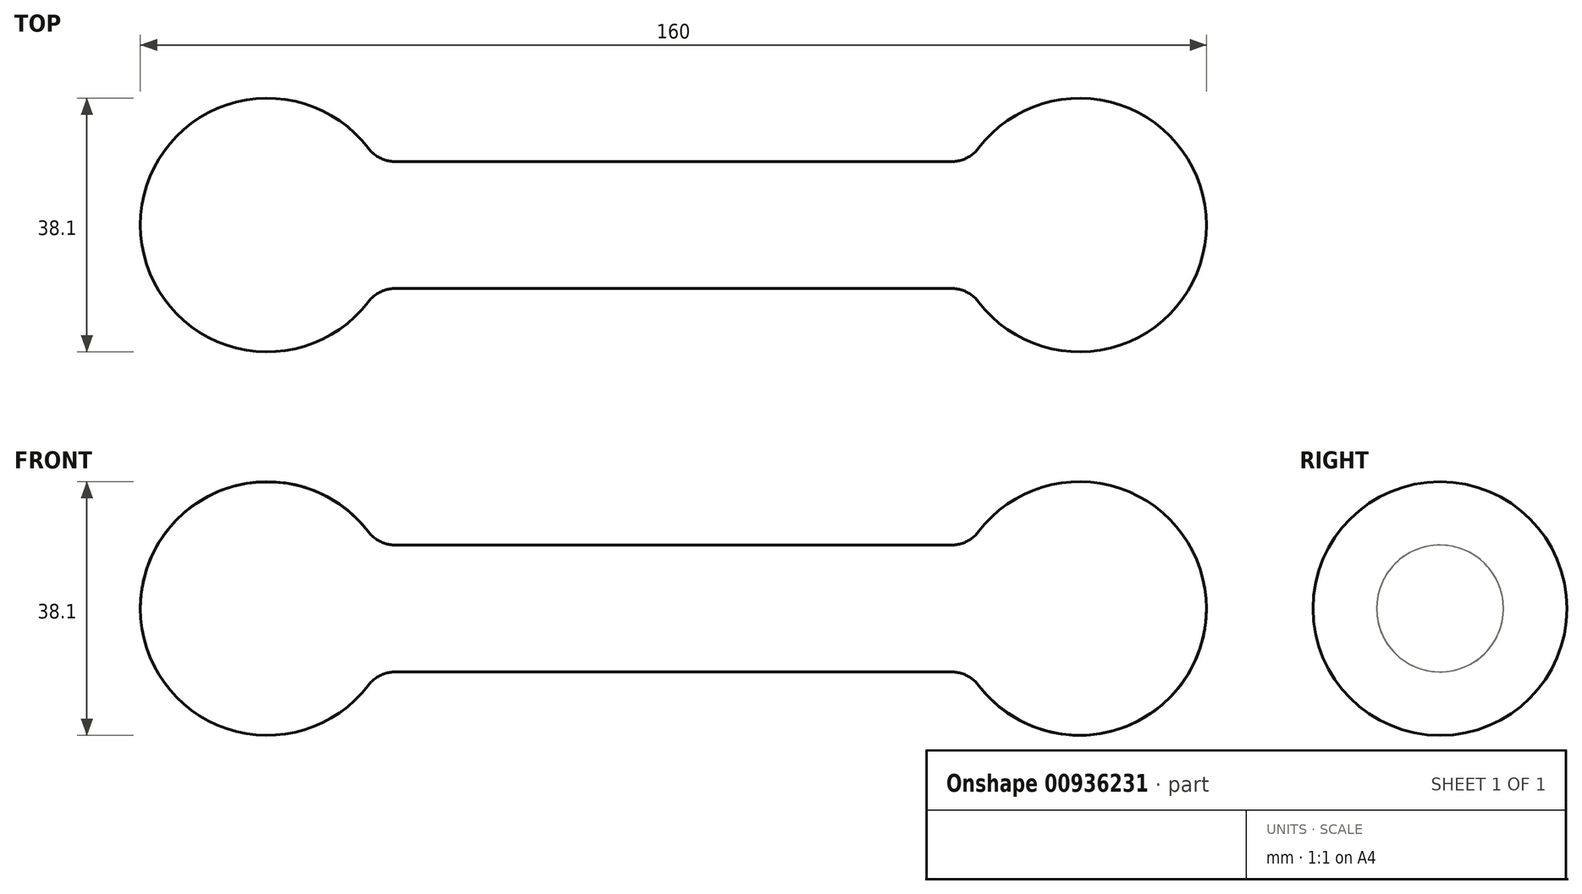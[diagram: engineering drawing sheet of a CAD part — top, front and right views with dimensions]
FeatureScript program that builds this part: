
annotation { "Feature Type Name" : "Feature", "Feature Type Description" : "" }
export const myFeature = defineFeature(function(context is Context, id is Id, definition is map)
    precondition{}
    {
        {
            var Q0;
            Q0=qCreatedBy(makeId("Front.planeOp"),FACE);
            var sketch = newSketch(context, id + "F0", { "sketchPlane" : qUnion([Q0])});
            skArc(sketch, "E0", {"start": v(-44.45, 9.53) * mm, "mid": v(-65.88, 18.4) * mm, "end": v(-80, 0) * mm});
            skLineSegment(sketch, "E1", {"start": v(-91.96, 0) * mm, "end": v(97.12, 0) * mm, "construction": true});
            skLineSegment(sketch, "E2", {"start": v(-44.45, 9.53) * mm, "end": v(0, 9.53) * mm});
            skPoint(sketch, "E3.orphan", {"position": v(-41.9, 0) * mm});
            skArc(sketch, "E4.MirrorCS", {"start": v(44.45, 9.53) * mm, "mid": v(65.88, 18.4) * mm, "end": v(80, 0) * mm});
            skLineSegment(sketch, "E5.MirrorCS", {"start": v(44.45, 9.53) * mm, "end": v(0, 9.53) * mm});
            skLineSegment(sketch, "E6", {"start": v(-80, 0) * mm, "end": v(80, 0) * mm});
            skSolve(sketch);
        }
        {
            var Q0;
            Q0=makeQuery(id+"F0.imprint","IMPRINT",FACE,{"disambiguationData":[TD([[makeQuery(id+"F0.imprint","IMPRINT",EDGE,{"derivedFrom":sQuery(id+"F0.wireOp",EDGE,"E0")}),1.0]])]});
            var Q1;
            Q1=sQuery(id+"F0.wireOp",EDGE,"E6");
            revolve(context, id + "F1", {"surfaceOperationType" : NewSurfaceOperationType.NEW, "entities" : qUnion([Q0]), "axis" : qUnion([Q1]), "revolveType" : RevolveType.FULL});
        }
        {
            var Q0;
            Q0=makeQuery(id+"F1.opRevolve","SWEPT_EDGE",EDGE,{"disambiguationData":[OSD([sQuery(id+"F0.wireOp",EDGE,"E4.MirrorCS"),sQuery(id+"F0.wireOp",EDGE,"E5.MirrorCS")])]});
            var Q1;
            Q1=makeQuery(id+"F1.opRevolve","SWEPT_EDGE",EDGE,{"disambiguationData":[OSD([sQuery(id+"F0.wireOp",EDGE,"E0"),sQuery(id+"F0.wireOp",EDGE,"E2")])]});
            fillet(context, id + "F2", {"entities" : qUnion([Q0, Q1]), "radius" : 5.08 * mm, "tangentPropagation" : true, "allowEdgeOverflow" : false});
        }
    });
